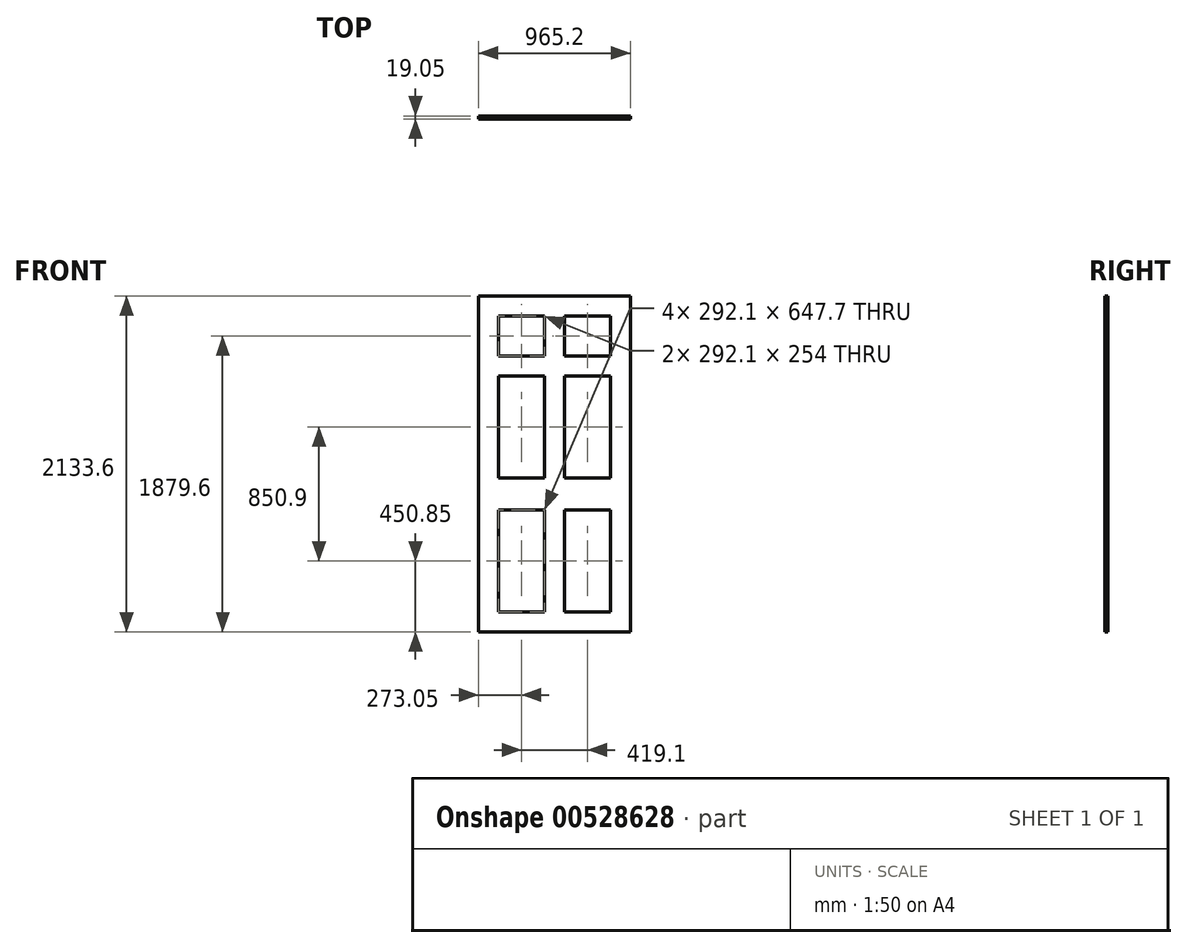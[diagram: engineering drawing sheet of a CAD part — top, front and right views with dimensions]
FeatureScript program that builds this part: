
annotation { "Feature Type Name" : "Feature", "Feature Type Description" : "" }
export const myFeature = defineFeature(function(context is Context, id is Id, definition is map)
    precondition{}
    {
        {
            var Q0;
            Q0=qCreatedBy(makeId("Front.planeOp"),FACE);
            var sketch = newSketch(context, id + "F0", { "sketchPlane" : qUnion([Q0])});
            skLineSegment(sketch, "E0.bottom", {"start": v(482.6, -1066.8) * mm, "end": v(-482.6, -1066.8) * mm});
            skLineSegment(sketch, "E0.top", {"start": v(482.6, 1066.8) * mm, "end": v(-482.6, 1066.8) * mm});
            skLineSegment(sketch, "E0.left", {"start": v(482.6, -1066.8) * mm, "end": v(482.6, 1066.8) * mm});
            skLineSegment(sketch, "E0.right", {"start": v(-482.6, -1066.8) * mm, "end": v(-482.6, 1066.8) * mm});
            skPoint(sketch, "E0.middle", {"position": v(0, 0) * mm});
            skLineSegment(sketch, "E1", {"start": v(-355.6, 939.8) * mm, "end": v(-355.6, -88.9) * mm});
            skLineSegment(sketch, "E2", {"start": v(-355.6, 939.8) * mm, "end": v(-63.5, 939.8) * mm});
            skPoint(sketch, "E3.orphan", {"position": v(-355.6, 1066.8) * mm});
            skLineSegment(sketch, "E4", {"start": v(355.6, 939.8) * mm, "end": v(355.6, 685.8) * mm});
            skPoint(sketch, "E5.orphan", {"position": v(482.6, 939.8) * mm});
            skLineSegment(sketch, "E6", {"start": v(-355.6, -939.8) * mm, "end": v(-63.5, -939.8) * mm});
            skPoint(sketch, "E7.orphan", {"position": v(-355.6, -1066.8) * mm});
            skPoint(sketch, "E8.orphan", {"position": v(355.6, -1066.8) * mm});
            skPoint(sketch, "E9.orphan", {"position": v(-482.6, -939.8) * mm});
            skLineSegment(sketch, "E10", {"start": v(-63.5, 939.8) * mm, "end": v(-63.5, 685.8) * mm});
            skLineSegment(sketch, "E11", {"start": v(63.5, -939.8) * mm, "end": v(63.5, -292.1) * mm});
            skLineSegment(sketch, "E12", {"start": v(-355.6, 685.8) * mm, "end": v(-63.5, 685.8) * mm});
            skLineSegment(sketch, "E13.trimOffspring", {"start": v(63.5, 939.8) * mm, "end": v(355.6, 939.8) * mm});
            skLineSegment(sketch, "E14.trimOffspring", {"start": v(63.5, 685.8) * mm, "end": v(355.6, 685.8) * mm});
            skLineSegment(sketch, "E15", {"start": v(-355.6, 558.8) * mm, "end": v(-63.5, 558.8) * mm});
            skLineSegment(sketch, "E16.trimOffspring", {"start": v(-63.5, 558.8) * mm, "end": v(-63.5, -88.9) * mm});
            skLineSegment(sketch, "E17.trimOffspring", {"start": v(63.5, 685.8) * mm, "end": v(63.5, 939.8) * mm});
            skLineSegment(sketch, "E18.trimOffspring", {"start": v(355.6, 558.8) * mm, "end": v(355.6, -88.9) * mm});
            skLineSegment(sketch, "E19.trimOffspring", {"start": v(63.5, 558.8) * mm, "end": v(355.6, 558.8) * mm});
            skLineSegment(sketch, "E20", {"start": v(-355.6, -88.9) * mm, "end": v(-63.5, -88.9) * mm});
            skLineSegment(sketch, "E21", {"start": v(-355.6, -292.1) * mm, "end": v(-63.5, -292.1) * mm});
            skLineSegment(sketch, "E22.trimOffspring", {"start": v(-63.5, -292.1) * mm, "end": v(-63.5, -939.8) * mm});
            skLineSegment(sketch, "E23.trimOffspring", {"start": v(63.5, -88.9) * mm, "end": v(355.6, -88.9) * mm});
            skLineSegment(sketch, "E24.trimOffspring", {"start": v(355.6, -292.1) * mm, "end": v(355.6, -939.8) * mm});
            skLineSegment(sketch, "E25.trimOffspring", {"start": v(63.5, -88.9) * mm, "end": v(63.5, 558.8) * mm});
            skLineSegment(sketch, "E26.trimOffspring", {"start": v(-355.6, -292.1) * mm, "end": v(-355.6, -939.8) * mm});
            skLineSegment(sketch, "E27.trimOffspring", {"start": v(63.5, -292.1) * mm, "end": v(355.6, -292.1) * mm});
            skLineSegment(sketch, "E28.trimOffspring", {"start": v(63.5, -939.8) * mm, "end": v(355.6, -939.8) * mm});
            skSolve(sketch);
        }
        {
            var Q0;
            Q0 = qSketchRegion(id + "F0", true);
            extrude(context, id + "F1", {"entities" : qUnion([Q0]), "depth" : 19.05 * mm, "offsetDistance" : 25.4 * mm});
        }
    });
